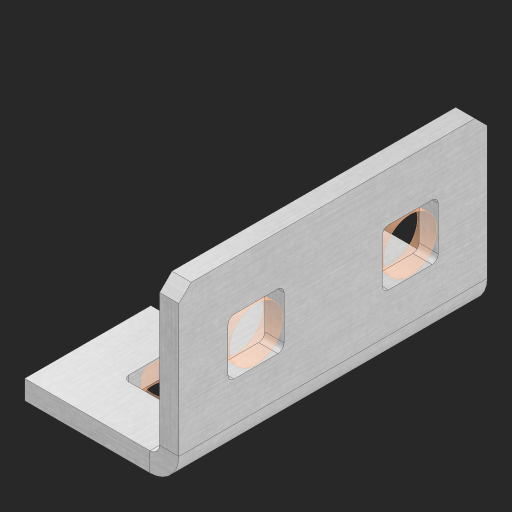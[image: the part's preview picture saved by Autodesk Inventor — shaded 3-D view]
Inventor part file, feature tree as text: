
AUTODESK INVENTOR PART (.ipt)
format: ipt  version: 2023 (Build 270158000, 158)  size: 550,400 bytes
history: native  units: in
note: dims shown in document units (in); Inventor stores cm internally (conversion verified against a paired STEP export)
features: other x154, sheet_metal_op x11, sketch x10, extrude x4, pattern_linear x2, mirror x1, chamfer x1
ambient origin geometry x8: Origin, YZ Plane, XZ Plane, XY Plane, X Axis, Y Axis, Z Axis, Center Point
bodies: Solid1 (feature_tree), Body (feature_tree)
feature tree (183):
  other  "Alu Half C 1x2x1x2"
  other  "Table"
  other  "Alu C 1x2x1x35"
  other  "Alu C 1x2x1x34"
  other  "Alu C 1x2x1x33"
  other  "Alu C 1x2x1x32"
  other  "Alu C 1x2x1x31"
  other  "Alu C 1x2x1x30"
  other  "Alu C 1x2x1x29"
  other  "Alu C 1x2x1x28"
  other  "Alu C 1x2x1x27"
  other  "Alu C 1x2x1x26"
  other  "Alu C 1x2x1x25"
  other  "Alu C 1x2x1x24"
  other  "Alu C 1x2x1x23"
  other  "Alu C 1x2x1x22"
  other  "Alu C 1x2x1x21"
  other  "Alu C 1x2x1x20"
  other  "Alu C 1x2x1x19"
  other  "Alu C 1x2x1x18"
  other  "Alu C 1x2x1x17"
  other  "Alu C 1x2x1x16"
  other  "Alu C 1x2x1x15"
  other  "Alu C 1x2x1x14"
  other  "Alu C 1x2x1x13"
  other  "Alu C 1x2x1x12"
  other  "Alu C 1x2x1x11"
  other  "Alu C 1x2x1x10"
  other  "Alu C 1x2x1x9"
  other  "Alu C 1x2x1x8"
  other  "Alu C 1x2x1x7"
  other  "Alu C 1x2x1x6"
  other  "Alu C 1x2x1x5"
  other  "Alu C 1x2x1x4"
  other  "Alu C 1x2x1x3"
  other  "Alu C 1x2x1x2"
  other  "Alu C 1x2x1x1"
  other  "Steel C 1x2x1x35"
  other  "Steel C 1x2x1x34"
  other  "Steel C 1x2x1x33"
  other  "Steel C 1x2x1x32"
  other  "Steel C 1x2x1x31"
  other  "Steel C 1x2x1x30"
  other  "Steel C 1x2x1x29"
  other  "Steel C 1x2x1x28"
  other  "Steel C 1x2x1x27"
  other  "Steel C 1x2x1x26"
  other  "Steel C 1x2x1x25"
  other  "Steel C 1x2x1x24"
  other  "Steel C 1x2x1x23"
  other  "Steel C 1x2x1x22"
  other  "Steel C 1x2x1x21"
  other  "Steel C 1x2x1x20"
  other  "Steel C 1x2x1x19"
  other  "Steel C 1x2x1x18"
  other  "Steel C 1x2x1x17"
  other  "Steel C 1x2x1x16"
  other  "Steel C 1x2x1x15"
  other  "Steel C 1x2x1x14"
  other  "Steel C 1x2x1x13"
  other  "Steel C 1x2x1x12"
  other  "Steel C 1x2x1x11"
  other  "Steel C 1x2x1x10"
  other  "Steel C 1x2x1x9"
  other  "Steel C 1x2x1x8"
  other  "Steel C 1x2x1x7"
  other  "Steel C 1x2x1x6"
  other  "Steel C 1x2x1x5"
  other  "Steel C 1x2x1x4"
  other  "Steel C 1x2x1x3"
  other  "Steel C 1x2x1x2"
  other  "Steel C 1x2x1x1"
  other  "Alu Half C 1x2x1x35"
  other  "Alu Half C 1x2x1x34"
  other  "Alu Half C 1x2x1x33"
  other  "Alu Half C 1x2x1x32"
  other  "Alu Half C 1x2x1x31"
  other  "Alu Half C 1x2x1x30"
  other  "Alu Half C 1x2x1x29"
  other  "Alu Half C 1x2x1x28"
  other  "Alu Half C 1x2x1x27"
  other  "Alu Half C 1x2x1x26"
  other  "Alu Half C 1x2x1x25"
  other  "Alu Half C 1x2x1x24"
  other  "Alu Half C 1x2x1x23"
  other  "Alu Half C 1x2x1x22"
  other  "Alu Half C 1x2x1x21"
  other  "Alu Half C 1x2x1x20"
  other  "Alu Half C 1x2x1x19"
  other  "Alu Half C 1x2x1x18"
  other  "Alu Half C 1x2x1x17"
  other  "Alu Half C 1x2x1x16"
  other  "Alu Half C 1x2x1x15"
  other  "Alu Half C 1x2x1x14"
  other  "Alu Half C 1x2x1x13"
  other  "Alu Half C 1x2x1x12"
  other  "Alu Half C 1x2x1x11"
  other  "Alu Half C 1x2x1x10"
  other  "Alu Half C 1x2x1x9"
  other  "Alu Half C 1x2x1x8"
  other  "Alu Half C 1x2x1x7"
  other  "Alu Half C 1x2x1x6"
  other  "Alu Half C 1x2x1x5"
  other  "Alu Half C 1x2x1x4"
  other  "Alu Half C 1x2x1x3"
  other  "Alu Half C 1x2x1x1"
  other  "Steel Half C 1x2x1x35"
  other  "Steel Half C 1x2x1x34"
  other  "Steel Half C 1x2x1x33"
  other  "Steel Half C 1x2x1x32"
  other  "Steel Half C 1x2x1x31"
  other  "Steel Half C 1x2x1x30"
  other  "Steel Half C 1x2x1x29"
  other  "Steel Half C 1x2x1x28"
  other  "Steel Half C 1x2x1x27"
  other  "Steel Half C 1x2x1x26"
  other  "Steel Half C 1x2x1x25"
  other  "Steel Half C 1x2x1x24"
  other  "Steel Half C 1x2x1x23"
  other  "Steel Half C 1x2x1x22"
  other  "Steel Half C 1x2x1x21"
  other  "Steel Half C 1x2x1x20"
  other  "Steel Half C 1x2x1x19"
  other  "Steel Half C 1x2x1x18"
  other  "Steel Half C 1x2x1x17"
  other  "Steel Half C 1x2x1x16"
  other  "Steel Half C 1x2x1x15"
  other  "Steel Half C 1x2x1x14"
  other  "Steel Half C 1x2x1x13"
  other  "Steel Half C 1x2x1x12"
  other  "Steel Half C 1x2x1x11"
  other  "Steel Half C 1x2x1x10"
  other  "Steel Half C 1x2x1x9"
  other  "Steel Half C 1x2x1x8"
  other  "Steel Half C 1x2x1x7"
  other  "Steel Half C 1x2x1x6"
  other  "Steel Half C 1x2x1x5"
  other  "Steel Half C 1x2x1x4"
  other  "Steel Half C 1x2x1x3"
  other  "Steel Half C 1x2x1x2"
  other  "Steel Half C 1x2x1x1"
  sheet_metal_op  "Flanges"
  other  "Flange Pattern Plane"
  other  "Flange Pattern Sketch"
  sheet_metal_op  "Flange Pattern"
  sheet_metal_op  "Body Pattern"
  pattern_linear  "Center Pattern"  Spacing1=0.0625in  [1 undecoded]
  other  "Arc Length"
  mirror  "Notch Mirror"
  pattern_linear  "Notch Pattern"  Spacing1=0.182in  [1 undecoded]
  chamfer  "End Chamfer"
  extrude  "Half Cut"  Depth=0.02in
  sketch  "Sketch1"  dims[d0=1.0in]
  other  "Plate1"
  sketch  "Sketch2"  dims[d1=1.0in]
  other  "Plate2"
  sheet_metal_op  "Bend1"
  sheet_metal_op  "Corner1"
  sketch  "Sketch3"  dims[d2=0.0625in]
  sketch  "Sketch7"  dims[d3=0.0625in]
  other  "Srf1"
  other  "Srf2"
  sketch  "Sketch8"  dims[d4=0.0312in]
  sketch  "Sketch9"  dims[d5=0.125in]
  other  "Srf91"
  sheet_metal_op  "Body Pattern Sketch"
  other  "Srf92"
  sketch  "Sketch13"  dims[d6=0.0625in]
  sketch  "Sketch14"  dims[d7=0.5in d8=90.0deg d9=0.0312in]
  sketch  "Sketch15"  dims[d10=0.25in]
  sketch  "Sketch16"  dims[d11=0.0625in d12=0.0625in d16=0.182in d17=0.02in d18=0.0625in d19=0.0in d20=0.25in d21=0.25in d38=0.7874in d40=0.5in d41=0.3937in d43=1.0in d46=0.172in d47=1.0in d48=0.0in d49=0.182in d50=0.02in d51=0.25in d52=0.25in d53=0.0625in d54=0.0in d55=0.172in d56=1.0in d57=0.0in d58=0.25in d60=0.7874in d62=0.5in d63=0.3937in d65=0.5in d85=0.1473in d86=0.1782in d88=0.04in d89=0.0625in d90=0.0in d91=0.04in d92=0.0491in d95=2.5in d96=0.04in d97=0.25in d98=45.0deg d99=0.25in d100=0.5in d101=0.0in d102=2.497in d106=0.182in d107=0.02in d108=0.5in d109=0.5in d110=0.0625in d111=0.0in d112=0.172in d113=0.5in d114=0.0in d117=0.5in d118=0.5in d119=0.5in]
  other  "Srf786"
  other  "Srf889"
  sheet_metal_op  "Flange Stamp"
  sheet_metal_op  "Flange Circle"
  sheet_metal_op  "Body Stamp"
  sheet_metal_op  "Body Circle"
  other  "Center Stamp"
  other  "Center Circle"
  sheet_metal_op  "Notch"
  extrude  "ExtrusionSrf2"  Depth=0.0625in
  extrude  "ExtrusionSrf92"  TaperAngle=0.0deg  [1 undecoded]
  extrude  "ExtrusionSrf889"  Depth=0.25in
note: 3 required parameter values undecoded (feature->parameter linkage not recoverable at this tier; creation-order binding heuristic only, values carry confidence <= 0.55)
